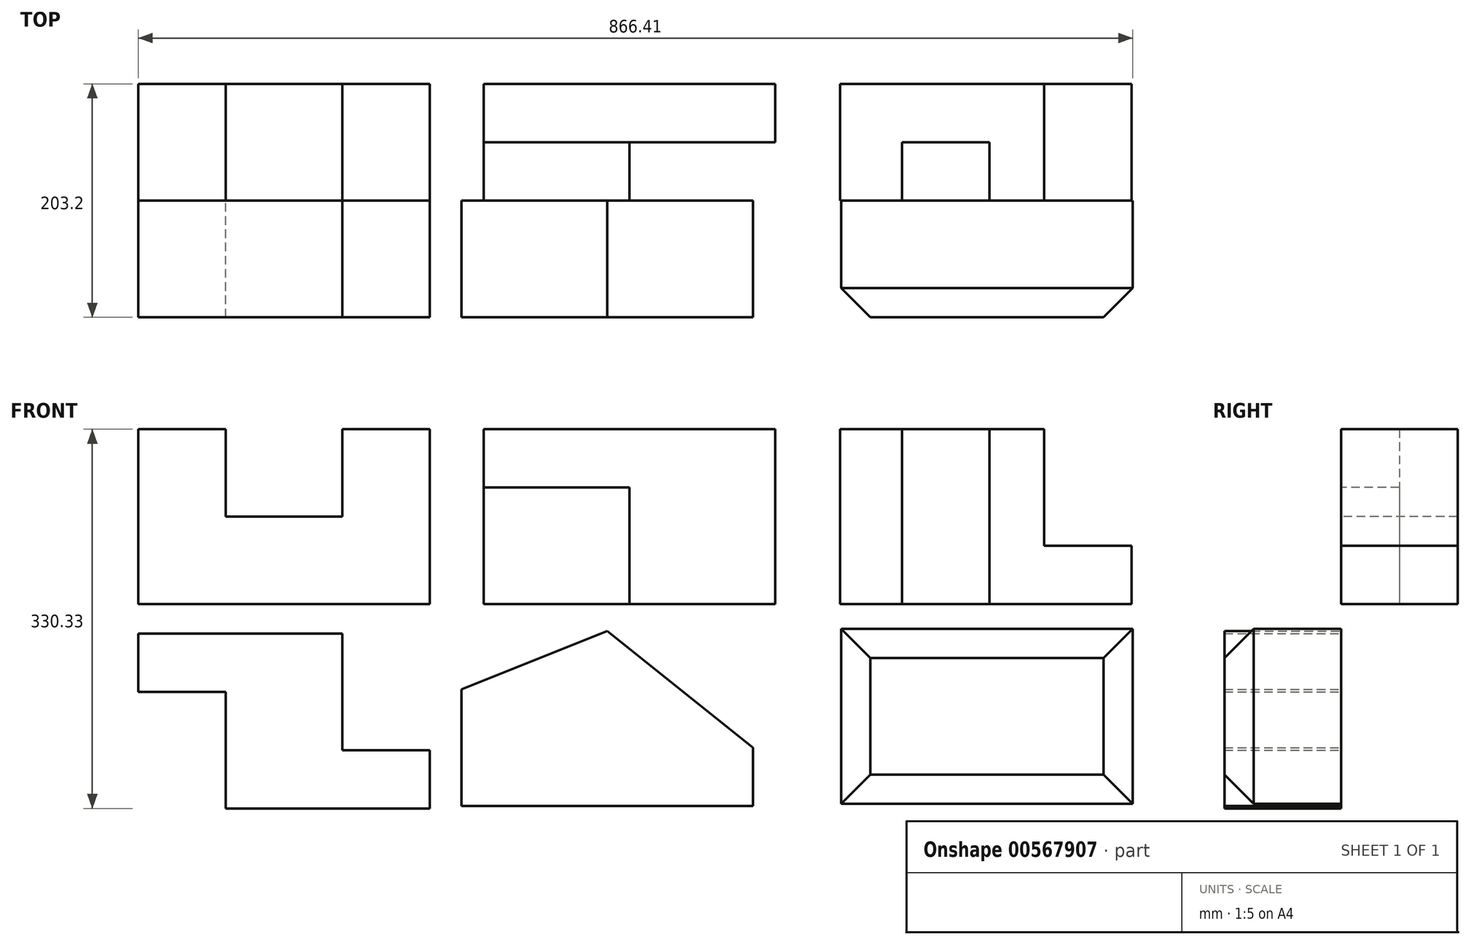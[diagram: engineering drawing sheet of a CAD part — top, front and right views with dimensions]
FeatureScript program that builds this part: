
annotation { "Feature Type Name" : "Feature", "Feature Type Description" : "" }
export const myFeature = defineFeature(function(context is Context, id is Id, definition is map)
    precondition{}
    {
        {
            var Q0;
            Q0=qCreatedBy(makeId("Front.planeOp"),FACE);
            var sketch = newSketch(context, id + "F0", { "sketchPlane" : qUnion([Q0])});
            skLineSegment(sketch, "E0", {"start": v(0, 0) * mm, "end": v(254, 0) * mm});
            skLineSegment(sketch, "E1", {"start": v(0, 0) * mm, "end": v(0, 152.4) * mm});
            skLineSegment(sketch, "E2", {"start": v(0, 152.4) * mm, "end": v(76.2, 152.4) * mm});
            skLineSegment(sketch, "E3", {"start": v(76.2, 152.4) * mm, "end": v(76.2, 76.2) * mm});
            skLineSegment(sketch, "E4", {"start": v(254, 0) * mm, "end": v(254, 152.4) * mm});
            skLineSegment(sketch, "E5", {"start": v(254, 152.4) * mm, "end": v(177.8, 152.4) * mm});
            skLineSegment(sketch, "E6", {"start": v(177.8, 152.4) * mm, "end": v(177.8, 76.2) * mm});
            skLineSegment(sketch, "E7", {"start": v(76.2, 76.2) * mm, "end": v(177.8, 76.2) * mm});
            skSolve(sketch);
        }
        {
            var Q0;
            Q0=makeQuery(id+"F0.imprint","IMPRINT",FACE,{"disambiguationData":[TD([[makeQuery(id+"F0.imprint","IMPRINT",EDGE,{"derivedFrom":sQuery(id+"F0.wireOp",EDGE,"E0")}),1.0]])]});
            extrude(context, id + "F1", {"entities" : qUnion([Q0]), "oppositeDirection" : true, "depth" : 101.6 * mm, "offsetDistance" : 25.4 * mm});
        }
        {
            var Q0;
            Q0=qCreatedBy(makeId("Top.planeOp"),FACE);
            var sketch = newSketch(context, id + "F2", { "sketchPlane" : qUnion([Q0])});
            skLineSegment(sketch, "E8", {"start": v(301.1, 0) * mm, "end": v(301.1, 101.6) * mm});
            skLineSegment(sketch, "E9", {"start": v(301.1, 101.6) * mm, "end": v(555.1, 101.6) * mm});
            skLineSegment(sketch, "E10", {"start": v(555.1, 101.6) * mm, "end": v(555.1, 50.8) * mm});
            skLineSegment(sketch, "E11", {"start": v(555.1, 50.8) * mm, "end": v(428.1, 50.8) * mm});
            skLineSegment(sketch, "E12", {"start": v(428.1, 50.8) * mm, "end": v(428.1, 0) * mm});
            skLineSegment(sketch, "E13", {"start": v(428.1, 0) * mm, "end": v(301.1, 0) * mm});
            skSolve(sketch);
        }
        {
            var Q0;
            Q0 = qSketchRegion(id + "F2", true);
            var Q1;
            Q1=makeQuery(id+"F2.imprint","IMPRINT",FACE,{"disambiguationData":[TD([[makeQuery(id+"F2.imprint","IMPRINT",EDGE,{"derivedFrom":sQuery(id+"F2.wireOp",EDGE,"E8")}),-1.0]])]});
            extrude(context, id + "F3", {"entities" : qUnion([Q0, Q1]), "depth" : 25.4 * mm, "offsetDistance" : 25.4 * mm});
        }
        {
            var Q0;
            Q0=makeQuery(id+"F3.opExtrude","CAP_FACE",FACE,{"disambiguationData":[OSD([sQuery(id+"F2.wireOp",EDGE,"E8"),sQuery(id+"F2.wireOp",EDGE,"E9"),sQuery(id+"F2.wireOp",EDGE,"E10"),sQuery(id+"F2.wireOp",EDGE,"E11"),sQuery(id+"F2.wireOp",EDGE,"E12"),sQuery(id+"F2.wireOp",EDGE,"E13")])],"isStart":false});
            extrude(context, id + "F4", {"entities" : qUnion([Q0]), "operationType" : NewBodyOperationType.ADD, "depth" : 127 * mm, "offsetDistance" : 25.4 * mm});
        }
        {
            var Q0;
            {var subQ0=sQuery(id+"F2.wireOp",EDGE,"E13");Q0=makeQuery(id+"F4.boolean.opBoolean","MERGE",FACE,{"derivedFrom":[makeQuery(id+"F3.opExtrude","SWEPT_FACE",FACE,{"disambiguationData":[OSD([subQ0])]}),makeQuery(id+"F4.opExtrude","SWEPT_FACE",FACE,{"disambiguationData":[OSD([subQ0])]})]});}
            var sketch = newSketch(context, id + "F5", { "sketchPlane" : qUnion([Q0])});
            skLineSegment(sketch, "E14.bottom", {"start": v(301.1, 152.4) * mm, "end": v(428.1, 152.4) * mm});
            skLineSegment(sketch, "E14.top", {"start": v(301.1, 101.6) * mm, "end": v(428.1, 101.6) * mm});
            skLineSegment(sketch, "E14.left", {"start": v(301.1, 152.4) * mm, "end": v(301.1, 101.6) * mm});
            skLineSegment(sketch, "E14.right", {"start": v(428.1, 152.4) * mm, "end": v(428.1, 101.6) * mm});
            skSolve(sketch);
        }
        {
            var Q0;
            Q0=makeQuery(id+"F5.imprint","IMPRINT",FACE,{"disambiguationData":[TD([[makeQuery(id+"F5.imprint","IMPRINT",EDGE,{"derivedFrom":sQuery(id+"F5.wireOp",EDGE,"E14.bottom")}),1.0]])]});
            extrude(context, id + "F6", {"entities" : qUnion([Q0]), "operationType" : NewBodyOperationType.REMOVE, "oppositeDirection" : true, "depth" : 50.8 * mm, "offsetDistance" : 25.4 * mm});
        }
        {
            var Q0;
            Q0=qCreatedBy(makeId("Front.planeOp"),FACE);
            var sketch = newSketch(context, id + "F7", { "sketchPlane" : qUnion([Q0])});
            skLineSegment(sketch, "E15", {"start": v(611.35, 0) * mm, "end": v(611.35, 152.4) * mm});
            skLineSegment(sketch, "E16", {"start": v(611.35, 152.4) * mm, "end": v(789.15, 152.4) * mm});
            skLineSegment(sketch, "E17", {"start": v(789.15, 152.4) * mm, "end": v(789.15, 50.8) * mm});
            skLineSegment(sketch, "E18", {"start": v(789.15, 50.8) * mm, "end": v(865.35, 50.8) * mm});
            skLineSegment(sketch, "E19", {"start": v(865.35, 50.8) * mm, "end": v(865.35, 0) * mm});
            skLineSegment(sketch, "E20", {"start": v(865.35, 0) * mm, "end": v(611.35, 0) * mm});
            skSolve(sketch);
        }
        {
            var Q0;
            Q0 = qSketchRegion(id + "F7", true);
            extrude(context, id + "F8", {"entities" : qUnion([Q0]), "oppositeDirection" : true, "depth" : 101.6 * mm, "offsetDistance" : 25.4 * mm});
        }
        {
            var Q0;
            Q0=makeQuery(id+"F8.opExtrude","SWEPT_FACE",FACE,{"disambiguationData":[OSD([sQuery(id+"F7.wireOp",EDGE,"E16")])]});
            var sketch = newSketch(context, id + "F9", { "sketchPlane" : qUnion([Q0])});
            skLineSegment(sketch, "E21.bottom", {"start": v(662.15, 0) * mm, "end": v(738.35, 0) * mm});
            skLineSegment(sketch, "E21.top", {"start": v(662.15, 50.8) * mm, "end": v(738.35, 50.8) * mm});
            skLineSegment(sketch, "E21.left", {"start": v(662.15, 0) * mm, "end": v(662.15, 50.8) * mm});
            skLineSegment(sketch, "E21.right", {"start": v(738.35, 0) * mm, "end": v(738.35, 50.8) * mm});
            skSolve(sketch);
        }
        {
            var Q0;
            Q0=makeQuery(id+"F9.imprint","IMPRINT",FACE,{"disambiguationData":[TD([[makeQuery(id+"F9.imprint","IMPRINT",EDGE,{"derivedFrom":sQuery(id+"F9.wireOp",EDGE,"E21.bottom")}),1.0]])]});
            extrude(context, id + "F10", {"entities" : qUnion([Q0]), "operationType" : NewBodyOperationType.ADD, "oppositeDirection" : true, "depth" : 152.4 * mm, "offsetDistance" : 25.4 * mm});
        }
        {
            var Q0;
            Q0=qCreatedBy(makeId("Front.planeOp"),FACE);
            var sketch = newSketch(context, id + "F11", { "sketchPlane" : qUnion([Q0])});
            skLineSegment(sketch, "E22", {"start": v(0, -25.53) * mm, "end": v(0, -76.33) * mm});
            skLineSegment(sketch, "E23", {"start": v(0, -76.33) * mm, "end": v(76.2, -76.33) * mm});
            skLineSegment(sketch, "E24", {"start": v(76.2, -76.33) * mm, "end": v(76.2, -177.93) * mm});
            skLineSegment(sketch, "E25", {"start": v(76.2, -177.93) * mm, "end": v(254, -177.93) * mm});
            skLineSegment(sketch, "E26", {"start": v(254, -177.93) * mm, "end": v(254, -127.13) * mm});
            skLineSegment(sketch, "E27", {"start": v(254, -127.13) * mm, "end": v(177.8, -127.13) * mm});
            skLineSegment(sketch, "E28", {"start": v(177.8, -127.13) * mm, "end": v(177.8, -25.53) * mm});
            skLineSegment(sketch, "E29", {"start": v(177.8, -25.53) * mm, "end": v(0, -25.53) * mm});
            skSolve(sketch);
        }
        {
            var Q0;
            Q0=makeQuery(id+"F11.imprint","IMPRINT",FACE,{"disambiguationData":[TD([[makeQuery(id+"F11.imprint","IMPRINT",EDGE,{"derivedFrom":sQuery(id+"F11.wireOp",EDGE,"E22")}),1.0]])]});
            extrude(context, id + "F12", {"entities" : qUnion([Q0]), "depth" : 101.6 * mm, "offsetDistance" : 25.4 * mm});
        }
        {
            var Q0;
            Q0=makeQuery(id+"F8.opExtrude","SWEPT_FACE",FACE,{"disambiguationData":[OSD([sQuery(id+"F7.wireOp",EDGE,"E16")])]});
            var sketch = newSketch(context, id + "F13", { "sketchPlane" : qUnion([Q0])});
            skLineSegment(sketch, "E30.bottom", {"start": v(665.47, 0) * mm, "end": v(741.67, 0) * mm});
            skLineSegment(sketch, "E30.top", {"start": v(665.47, 50.8) * mm, "end": v(741.67, 50.8) * mm});
            skLineSegment(sketch, "E30.left", {"start": v(665.47, 0) * mm, "end": v(665.47, 50.8) * mm});
            skLineSegment(sketch, "E30.right", {"start": v(741.67, 0) * mm, "end": v(741.67, 50.8) * mm});
            skSolve(sketch);
        }
        {
            var Q0;
            Q0=makeQuery(id+"F13.imprint","IMPRINT",FACE,{"disambiguationData":[TD([[makeQuery(id+"F13.imprint","IMPRINT",EDGE,{"derivedFrom":sQuery(id+"F13.wireOp",EDGE,"E30.bottom")}),1.0]])]});
            extrude(context, id + "F14", {"entities" : qUnion([Q0]), "operationType" : NewBodyOperationType.REMOVE, "oppositeDirection" : true, "depth" : 152.4 * mm, "offsetDistance" : 25.4 * mm});
        }
        {
            var Q0;
            Q0=qCreatedBy(makeId("Front.planeOp"),FACE);
            var sketch = newSketch(context, id + "F15", { "sketchPlane" : qUnion([Q0])});
            skLineSegment(sketch, "E31", {"start": v(281.47, -175.75) * mm, "end": v(281.47, -74.15) * mm});
            skLineSegment(sketch, "E32", {"start": v(535.47, -124.95) * mm, "end": v(535.47, -175.75) * mm});
            skLineSegment(sketch, "E33", {"start": v(535.47, -175.75) * mm, "end": v(281.47, -175.75) * mm});
            skLineSegment(sketch, "E34", {"start": v(281.47, -74.15) * mm, "end": v(408.47, -23.35) * mm});
            skLineSegment(sketch, "E35", {"start": v(535.47, -124.95) * mm, "end": v(408.47, -23.35) * mm});
            skSolve(sketch);
        }
        {
            var Q0;
            Q0=makeQuery(id+"F15.imprint","IMPRINT",FACE,{"disambiguationData":[TD([[makeQuery(id+"F15.imprint","IMPRINT",EDGE,{"derivedFrom":sQuery(id+"F15.wireOp",EDGE,"E31")}),-1.0]])]});
            extrude(context, id + "F16", {"entities" : qUnion([Q0]), "depth" : 101.6 * mm, "offsetDistance" : 25.4 * mm});
        }
        {
            var Q0;
            Q0=qCreatedBy(makeId("Front.planeOp"),FACE);
            var sketch = newSketch(context, id + "F17", { "sketchPlane" : qUnion([Q0])});
            skLineSegment(sketch, "E36", {"start": v(612.4, -174.07) * mm, "end": v(612.4, -21.67) * mm});
            skLineSegment(sketch, "E37", {"start": v(612.4, -21.67) * mm, "end": v(866.4, -21.67) * mm});
            skLineSegment(sketch, "E38", {"start": v(866.4, -21.67) * mm, "end": v(866.4, -174.07) * mm});
            skLineSegment(sketch, "E39", {"start": v(866.4, -174.07) * mm, "end": v(612.4, -174.07) * mm});
            skSolve(sketch);
        }
        {
            var Q0;
            Q0 = qSketchRegion(id + "F17", true);
            extrude(context, id + "F18", {"entities" : qUnion([Q0]), "depth" : 101.6 * mm, "offsetDistance" : 25.4 * mm});
        }
        {
            var Q0;
            Q0=makeQuery(id+"F18.opExtrude","CAP_FACE",FACE,{"disambiguationData":[OSD([sQuery(id+"F17.wireOp",EDGE,"E36"),sQuery(id+"F17.wireOp",EDGE,"E37"),sQuery(id+"F17.wireOp",EDGE,"E38"),sQuery(id+"F17.wireOp",EDGE,"E39")])],"isStart":false});
            chamfer(context, id + "F19", {"entities" : qUnion([Q0]), "width" : 25.4 * mm, "tangentPropagation" : true});
        }
    });
